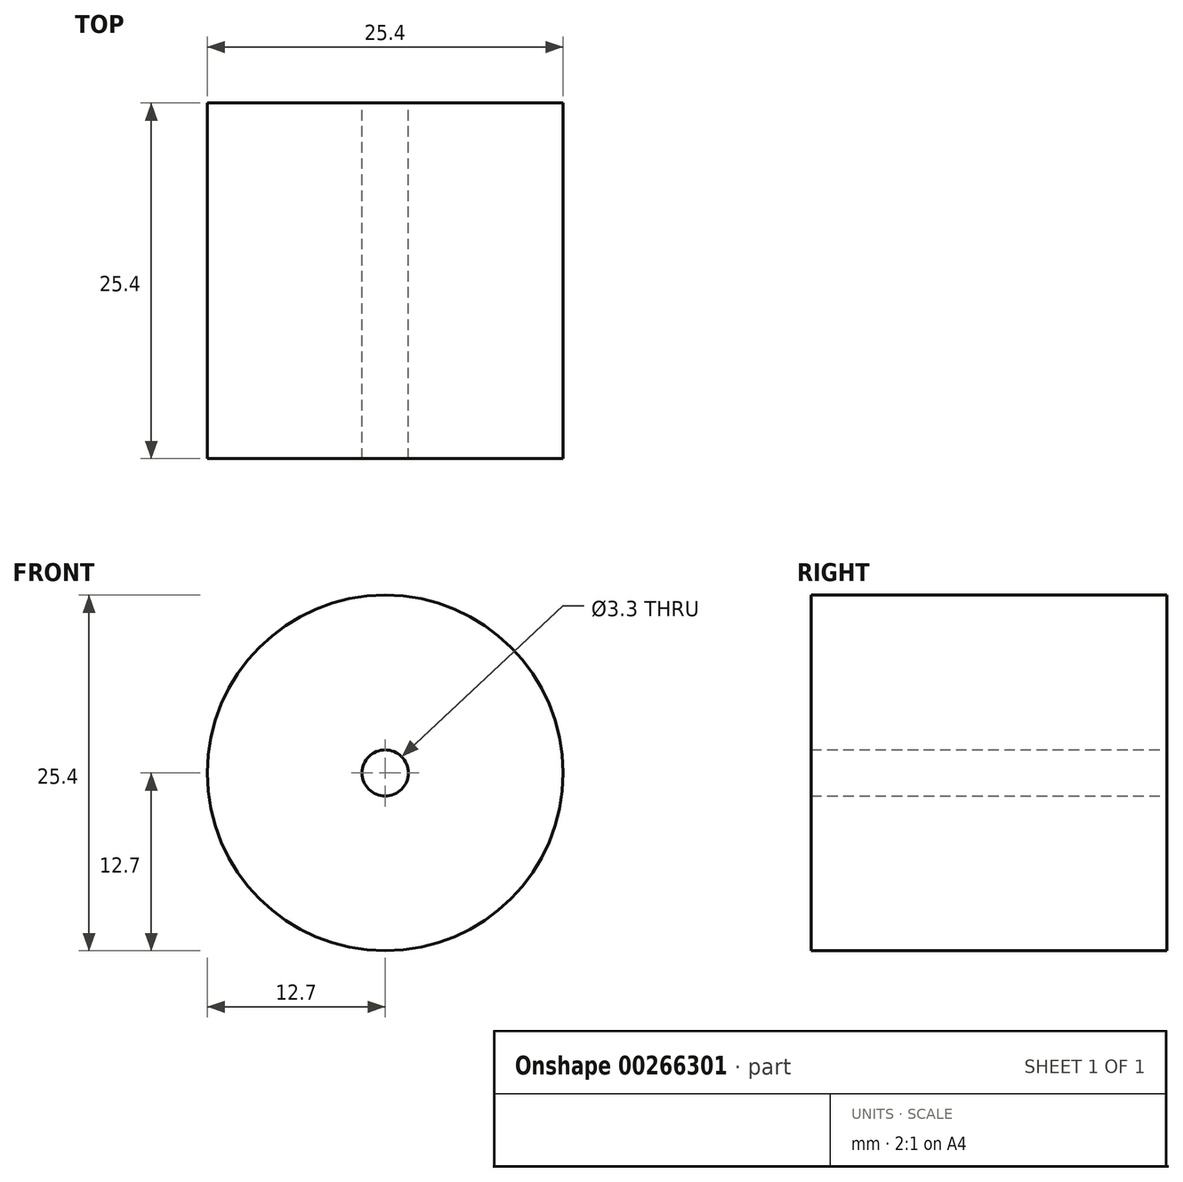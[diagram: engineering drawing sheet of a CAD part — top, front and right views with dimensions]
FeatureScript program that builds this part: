
annotation { "Feature Type Name" : "Feature", "Feature Type Description" : "" }
export const myFeature = defineFeature(function(context is Context, id is Id, definition is map)
    precondition{}
    {
        {
            var Q0;
            Q0=qCreatedBy(makeId("Front.planeOp"),FACE);
            var sketch = newSketch(context, id + "F0", { "sketchPlane" : qUnion([Q0])});
            skCircle(sketch, "E0", {"center": v(0, 0) * mm, "radius": 12.7 * mm});
            skCircle(sketch, "E1", {"center": v(0, 0) * mm, "radius": 1.65 * mm});
            skSolve(sketch);
        }
        {
            var Q0;
            Q0=makeQuery(id+"F0.imprint","IMPRINT",FACE,{"disambiguationData":[TD([[makeQuery(id+"F0.imprint","IMPRINT",EDGE,{"derivedFrom":sQuery(id+"F0.wireOp",EDGE,"E0")}),1.0]])]});
            extrude(context, id + "F1", {"entities" : qUnion([Q0]), "depth" : 25.4 * mm});
        }
    });
